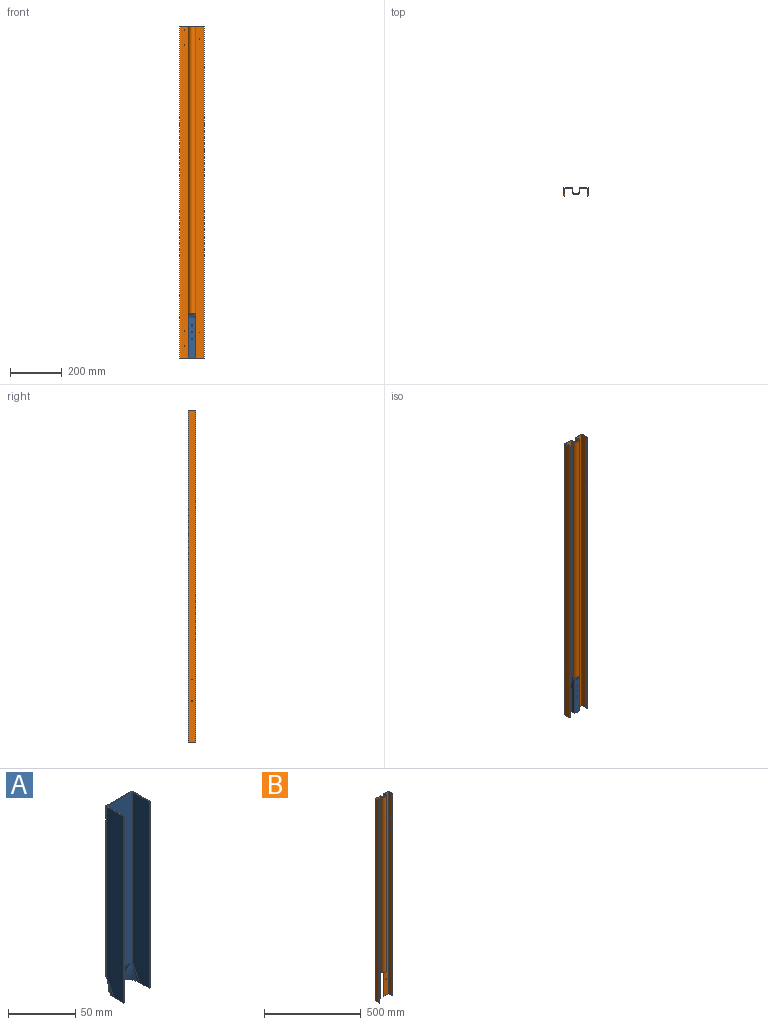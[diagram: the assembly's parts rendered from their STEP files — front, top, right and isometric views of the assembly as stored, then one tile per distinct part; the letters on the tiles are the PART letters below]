
ASSEMBLY  parts=2 mates=1
PART A: 27 faces, bbox 35.2x31.2x177.2 mm
  f0: cylinder r=2.75mm len=5.5mm, axis (0,1,0), area 17.3mm2, adj f5,f17
  f1: cylinder r=2.75mm len=5.5mm, axis (0,1,0), area 17.3mm2, adj f5,f17
  f2: cylinder r=2.75mm len=5.5mm, axis (0,1,0), area 17.3mm2, adj f5,f17
  f3: cylinder r=2mm len=155mm, axis (0,0,1), area 76mm2, adj f5,f7,f12,f13
  f4: cylinder r=2mm len=155mm, axis (0,0,1), area 76mm2, adj f5,f10,f11,f13
  f5: plane 155.16x25.88mm, normal (0,-1,0), area 3944.4mm2, adj f0,f1,f2,f3,f4,f6,f7,f11
  f6: plane 31.84x20.86mm, normal (0,-0.95,-0.32), area 252.1mm2, adj f5,f7,f8,f9,f11,f22
  f7: bspline ~15.36x9.22mm, area 39.2mm2, adj f3,f5,f6,f8,f12,f22
  f8: bspline ~13.47x11.57mm, area 74.8mm2, adj f6,f7,f22
  f9: bspline ~13.47x11.57mm, area 74.8mm2, adj f6,f11,f22
  f10: plane 170x17.51mm, normal (1,0,0), area 2921.1mm2, adj f4,f11,f13,f22,f23
  f11: bspline ~15.36x9.22mm, area 39.2mm2, adj f4,f5,f6,f9,f10,f22
  f12: plane 170x17.51mm, normal (-1,0,0), area 2921.1mm2, adj f3,f7,f13,f14,f22
  f13: plane 28x19mm, normal (0,0,1), area 63.6mm2, adj f3,f4,f5,f10,f12,f14,f15,f16
  f14: plane 170x1mm, normal (0,-1,0), area 170mm2, adj f12,f13,f22,f26
  f15: cylinder r=3mm len=155mm, axis (0,0,1), area 240.9mm2, adj f13,f17,f19,f26
  f16: cylinder r=3mm len=155mm, axis (0,0,1), area 240.9mm2, adj f13,f17,f24,f25
  f17: plane 155x27.21mm, normal (0,1,0), area 4146.7mm2, adj f0,f1,f2,f13,f15,f16,f18
  f18: plane 34.37x22.16mm, normal (0,0.95,0.32), area 265.2mm2, adj f17,f19,f20,f21,f25
  f19: bspline ~15x9.97mm, area 49.2mm2, adj f15,f18,f20,f22,f26
  f20: bspline ~13.73x13.57mm, area 89.1mm2, adj f18,f19,f22
  f21: bspline ~13.7x13.48mm, area 89.1mm2, adj f18,f22,f25
  f22: plane 34.23x30.23mm, normal (0,0,-1), area 62.5mm2, adj f6,f7,f8,f9,f10,f11,f12,f14
  f23: plane 170x1mm, normal (0,-1,0), area 170mm2, adj f10,f13,f22,f24
  f24: plane 170x17.51mm, normal (-1,0,0), area 2921.1mm2, adj f13,f16,f22,f23,f25
  f25: bspline ~15x9.97mm, area 49.2mm2, adj f16,f18,f21,f22,f24
  f26: plane 170x17.51mm, normal (1,0,0), area 2921.1mm2, adj f13,f14,f15,f19,f22
PART B: 38 faces, bbox 93x29x1282 mm
  f0: plane 1112x10mm, normal (-1,0,0), area 11120mm2, adj f1,f7,f16,f37
  f1: cylinder r=14mm len=1112mm, axis (0,0,-1), area 48908.3mm2, adj f0,f2,f7,f37
  f2: plane 1112x10mm, normal (1,0,0), area 11120mm2, adj f1,f7,f17,f37
  f3: plane 1282x11mm, normal (-1,0,0), area 12402mm2, adj f4,f6,f7,f17,f25,f37
  f4: cylinder r=13mm len=1112mm, axis (0,0,-1), area 45414.9mm2, adj f3,f5,f7,f37
  f5: plane 1282x11mm, normal (1,0,0), area 12402mm2, adj f4,f7,f8,f16,f26,f37
  f6: plane 33.5x29mm, normal (0,0,-1), area 68.6mm2, adj f3,f17,f18,f19,f20,f21,f22,f23
  f7: plane 93x29mm, normal (0,0,1), area 199.7mm2, adj f0,f1,f2,f3,f4,f5,f8,f9
  f8: plane 1282x33.5mm, normal (0,1,0), area 42918.7mm2, adj f5,f7,f9,f26,f28,f29,f35,f36
  f9: plane 1282x27.5mm, normal (-1,0,0), area 35240.9mm2, adj f7,f8,f10,f26,f30,f31
  f10: cylinder r=1.5mm len=1282mm, axis (0,0,-1), area 6365.3mm2, adj f7,f9,f11,f26
  f11: plane 1282x5.25mm, normal (0.99,0.17,0), area 6825.2mm2, adj f7,f10,f12,f26
  f12: plane 1282x0.99mm, normal (-0.17,0.99,0), area 1282mm2, adj f7,f11,f13,f26
  f13: plane 1282x5.25mm, normal (-0.99,-0.17,0), area 6825.2mm2, adj f7,f12,f14,f26
  f14: cylinder r=0.5mm len=1282mm, axis (0,0,-1), area 2121.8mm2, adj f7,f13,f15,f26
  f15: plane 1282x26.5mm, normal (1,0,0), area 33958.9mm2, adj f7,f14,f16,f26,f30,f31
  f16: plane 1282x32.5mm, normal (0,-1,0), area 40524.7mm2, adj f0,f5,f7,f15,f26,f28,f29,f35
  f17: plane 1282x32.5mm, normal (0,-1,0), area 40538.9mm2, adj f2,f3,f6,f7,f18,f27,f34,f37
  f18: plane 1282x26.5mm, normal (-1,0,0), area 33958.9mm2, adj f6,f7,f17,f19,f32,f33
  f19: cylinder r=0.5mm len=1282mm, axis (0,0,-1), area 2121.8mm2, adj f6,f7,f18,f20
  f20: plane 1282x5.25mm, normal (0.99,-0.17,0), area 6825.2mm2, adj f6,f7,f19,f21
  f21: plane 1282x0.99mm, normal (0.17,0.99,0), area 1282mm2, adj f6,f7,f20,f22
  f22: plane 1282x5.25mm, normal (-0.99,0.17,0), area 6825.2mm2, adj f6,f7,f21,f23
  f23: cylinder r=1.5mm len=1282mm, axis (0,0,-1), area 6365.3mm2, adj f6,f7,f22,f24
  f24: plane 1282x27.5mm, normal (1,0,0), area 35240.9mm2, adj f6,f7,f23,f25,f32,f33
  f25: plane 1282x33.5mm, normal (0,1,0), area 42932.9mm2, adj f3,f6,f7,f24,f27,f34
  f26: plane 33.5x29mm, normal (0,0,-1), area 68.6mm2, adj f5,f8,f9,f10,f11,f12,f13,f14
  f27: cylinder r=1.5mm len=3mm, axis (0,-1,0), area 9.4mm2, adj f17,f25
  f28: cylinder r=1.5mm len=3mm, axis (0,-1,0), area 9.4mm2, adj f8,f16
  f29: cylinder r=1.5mm len=3mm, axis (0,-1,0), area 9.4mm2, adj f8,f16
  f30: cylinder r=1.5mm len=3mm, axis (1,0,0), area 9.4mm2, adj f9,f15
  f31: cylinder r=1.5mm len=3mm, axis (1,0,0), area 9.4mm2, adj f9,f15
  f32: cylinder r=1.5mm len=3mm, axis (1,0,0), area 9.4mm2, adj f18,f24
  f33: cylinder r=1.5mm len=3mm, axis (1,0,0), area 9.4mm2, adj f18,f24
  f34: cylinder r=1.5mm len=3mm, axis (0,-1,0), area 9.4mm2, adj f17,f25
  f35: cylinder r=1.5mm len=3mm, axis (0,-1,0), area 9.4mm2, adj f8,f16
  f36: cylinder r=1.5mm len=3mm, axis (0,-1,0), area 9.4mm2, adj f8,f16
  f37: plane 28x24mm, normal (0,0,-1), area 62.4mm2, adj f0,f1,f2,f3,f4,f5,f16,f17
PLACE A rot(axis=(1,0,0),180deg) t=(1148.98,430.22,-621.81)mm
PLACE B t=(-1.02,0.22,-791.81)mm fixed
MATE fastened A.f22 <-> B.f37  axis (0,0,1) through (1162.98,440.22,-621.81)mm
